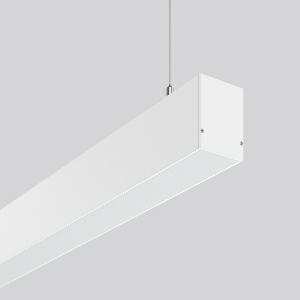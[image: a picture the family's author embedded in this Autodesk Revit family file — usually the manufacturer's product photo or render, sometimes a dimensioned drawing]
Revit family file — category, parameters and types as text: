
# Revit family: less_is_more_50_312314_002_1_a6c4
name_source: partatom
category: Lighting Fixtures
units: mm (PartAtom-declared; Revit-internal decimal feet)

## family parameters
Cut with Voids When Loaded = No
Host = Face
Light Source = No
Part Type = Normal
Room Calculation Point = No
Round Connector Dimension = Use Diameter
Shared = No

## types (1)
- LESS IS MORE 50 (1 x LED Modul 840, 4850 lm, 4000)
    Apparent Load = 40 VA
    CIE Flux Codes = 48 79 95 100 100
    Color Rendering = 80
    Color Temperature = 4000
    Default Elevation = 1800 mm
    Description = Series: LESS IS MORE 50
Linear pendant luminaire for aesthetically sophisticated lighting. Housing: extruded aluminium profile, powder-coated. End cap aluminium powder-coated. Canopy made of aluminium, powder-coated. Diffuser made of non-yellowing plastic (PMMA), opal. Direct light emission. Suitable for pendant. 2-point steel cable suspension freely positionable and infinitely height-adjustable. Special lengths available on request. LED unit with integrated converter interchangeable and removable. Suitable for through-wiring. With sensors or as a safety luminaire on request. 
Colour: traffic white, matt (RAL 9016)
Length: 1687 mm
Width: 57 mm
Height: 75 mm
Suspension length: 2000 mm
Lamp: LED
Socket: without socket
Colour temperature: 4000K
Colour rendering index (CRI): 80
System power: 40 W
Rated luminous flux: 4850 lm
Luminous efficiency: 121 lm/W
Control gear: Regulated power supply
Protection class: I
Type of protection: IP 20
    Height = 75 mm
    Lamp = 1 x LED Modul 840
    Lamp Light Flux = 4850 lm
    Lamp count = 1
    Length = 1687 mm
    Lifetime = 50000 h
    Luminous efficacy = 121 lm/W
    Manufacturer = RZB
    ModVariant = No
    Model = 312314.002.1
    Mounting Place = Ceiling
    Mounting Type = Pendant
    Number of Poles = 1
    OnlyDefault = Yes
    Power Factor = 1
    Product Name = LESS IS MORE 50
    Product group = Pendant LED linear luminaires
    ProductGroupID = 907
    Protection Class = Protection class I
    Protection Degree = IP 20
    RLX_Detail_Level = 1
    RLX_Emergency_Light_Flux = 0 lm
    RLX_Emergency_Type = 0
    RLX_Emergency_Type_DB = No
    RlxData = <blob elided: 20589 chars, md5=353cb90c>
    Socket = socket
    Standby Power = 0 W
    System Light Flux = 4850 lm
    System Power = 40 W
    Type Comments = Product without accessories
    Type Image = 312318.002.jpg
    URL = http://relux.com
    VarID = ---
    Voltage = 230 V
    Voltage Range = 220-240 V
    Weight = 0.00 kg
    Width = 57 mm

## geometry (parser evidence)
native form markers: Blend x4, Sweep x11
no freeform markers — native parametric forms only
